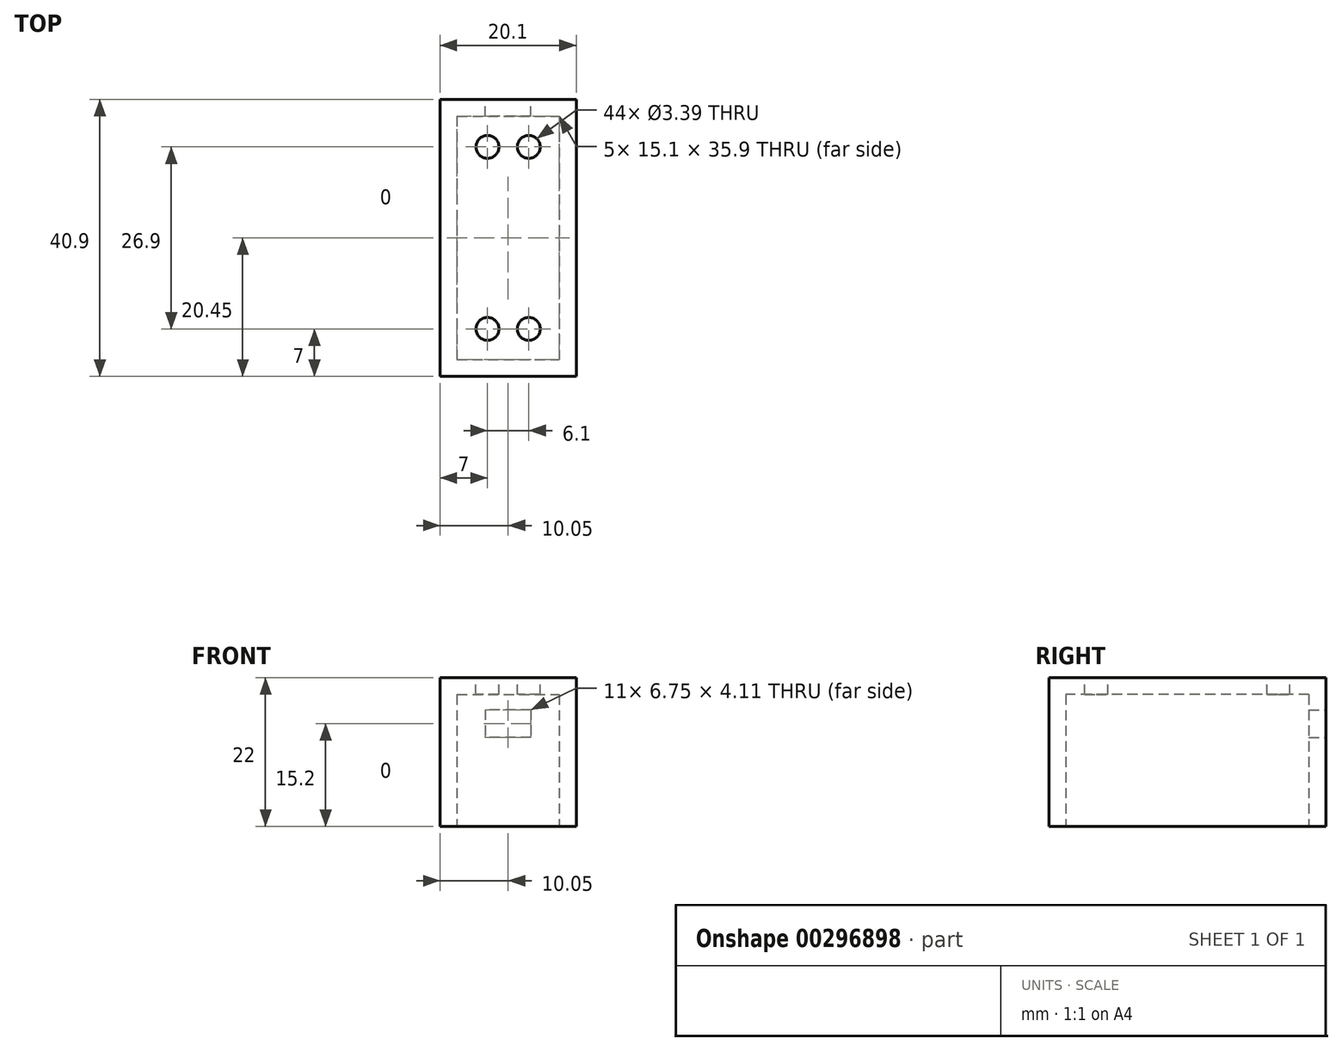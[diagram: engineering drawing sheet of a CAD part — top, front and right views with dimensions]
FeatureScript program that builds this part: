
annotation { "Feature Type Name" : "Feature", "Feature Type Description" : "" }
export const myFeature = defineFeature(function(context is Context, id is Id, definition is map)
    precondition{}
    {
        {
            var Q0;
            Q0=qCreatedBy(makeId("Top.planeOp"),FACE);
            var sketch = newSketch(context, id + "F0", { "sketchPlane" : qUnion([Q0])});
            skLineSegment(sketch, "E0", {"start": v(17.6, 44.65) * mm, "end": v(-2.5, 44.65) * mm});
            skLineSegment(sketch, "E1", {"start": v(17.6, 3.75) * mm, "end": v(-2.5, 3.75) * mm});
            skLineSegment(sketch, "E2", {"start": v(-2.5, 44.65) * mm, "end": v(-2.5, 3.75) * mm});
            skLineSegment(sketch, "E3", {"start": v(17.6, 44.65) * mm, "end": v(17.6, 3.75) * mm});
            skLineSegment(sketch, "E4.bottom", {"start": v(0, 42.15) * mm, "end": v(15.1, 42.15) * mm});
            skLineSegment(sketch, "E4.top", {"start": v(0, 6.25) * mm, "end": v(15.1, 6.25) * mm});
            skLineSegment(sketch, "E4.left", {"start": v(0, 42.15) * mm, "end": v(0, 6.25) * mm});
            skLineSegment(sketch, "E4.right", {"start": v(15.1, 42.15) * mm, "end": v(15.1, 6.25) * mm});
            skSolve(sketch);
        }
        {
            var Q0;
            Q0=makeQuery(id+"F0.imprint","IMPRINT",FACE,{"disambiguationData":[TD([[makeQuery(id+"F0.imprint","IMPRINT",EDGE,{"derivedFrom":sQuery(id+"F0.wireOp",EDGE,"E0")}),1.0]])]});
            var Q1;
            Q1=makeQuery(id+"F0.imprint","IMPRINT",FACE,{"disambiguationData":[TD([[makeQuery(id+"F0.imprint","IMPRINT",EDGE,{"derivedFrom":sQuery(id+"F0.wireOp",EDGE,"E4.bottom")}),-1.0]])]});
            extrude(context, id + "F1", {"entities" : qUnion([Q0, Q1]), "depth" : 22 * mm});
        }
        {
            var Q0;
            Q0=makeQuery(id+"F0.imprint","IMPRINT",FACE,{"disambiguationData":[TD([[makeQuery(id+"F0.imprint","IMPRINT",EDGE,{"derivedFrom":sQuery(id+"F0.wireOp",EDGE,"E4.bottom")}),-1.0]])]});
            extrude(context, id + "F2", {"entities" : qUnion([Q0]), "operationType" : NewBodyOperationType.REMOVE, "depth" : 19.5 * mm});
        }
        {
            var Q0;
            Q0=makeQuery(id+"F1.opExtrude","CAP_FACE",FACE,{"disambiguationData":[OSD([sQuery(id+"F0.wireOp",EDGE,"E0"),sQuery(id+"F0.wireOp",EDGE,"E1"),sQuery(id+"F0.wireOp",EDGE,"E2"),sQuery(id+"F0.wireOp",EDGE,"E3")])],"isStart":false});
            cPlane(context, id + "F3", {"entities" : qUnion([Q0]), "cplaneType" : CPlaneType.OFFSET, "offset" : 0 * mm, "width" : 150 * mm, "height" : 150 * mm});
        }
        {
            var Q0;
            Q0=qCreatedBy(id+"F3.planeOp",FACE);
            var sketch = newSketch(context, id + "F4", { "sketchPlane" : qUnion([Q0])});
            skLineSegment(sketch, "E5.bottom", {"start": v(10.6, 10.75) * mm, "end": v(4.5, 10.75) * mm, "construction": true});
            skLineSegment(sketch, "E5.top", {"start": v(10.6, 37.65) * mm, "end": v(4.5, 37.65) * mm, "construction": true});
            skLineSegment(sketch, "E5.left", {"start": v(10.6, 10.75) * mm, "end": v(10.6, 37.65) * mm, "construction": true});
            skLineSegment(sketch, "E5.right", {"start": v(4.5, 10.75) * mm, "end": v(4.5, 37.65) * mm, "construction": true});
            skCircle(sketch, "E6", {"center": v(4.5, 37.65) * mm, "radius": 1.7 * mm});
            skCircle(sketch, "E7", {"center": v(10.6, 37.65) * mm, "radius": 1.7 * mm});
            skCircle(sketch, "E8", {"center": v(4.5, 10.75) * mm, "radius": 1.7 * mm});
            skCircle(sketch, "E9", {"center": v(10.6, 10.75) * mm, "radius": 1.7 * mm});
            skSolve(sketch);
        }
        {
            var Q0;
            Q0 = qSketchRegion(id + "F4", true);
            extrude(context, id + "F5", {"entities" : qUnion([Q0]), "operationType" : NewBodyOperationType.REMOVE, "oppositeDirection" : true, "depth" : 25 * mm});
        }
        {
            var Q0;
            Q0=makeQuery(id+"F1.opExtrude","SWEPT_FACE",FACE,{"disambiguationData":[OSD([sQuery(id+"F0.wireOp",EDGE,"E0")])]});
            cPlane(context, id + "F6", {"entities" : qUnion([Q0]), "cplaneType" : CPlaneType.OFFSET, "offset" : 0 * mm, "width" : 150 * mm, "height" : 150 * mm});
        }
        {
            var Q0;
            Q0=qCreatedBy(id+"F6.planeOp",FACE);
            var sketch = newSketch(context, id + "F7", { "sketchPlane" : qUnion([Q0])});
            skPoint(sketch, "E10", {"position": v(-7.55, 15.2) * mm});
            skLineSegment(sketch, "E11.bottom", {"start": v(-7.55, 17.25) * mm, "end": v(-4.17, 17.25) * mm});
            skLineSegment(sketch, "E11.top", {"start": v(-7.55, 13.14) * mm, "end": v(-4.17, 13.14) * mm});
            skLineSegment(sketch, "E11.left", {"start": v(-7.55, 17.25) * mm, "end": v(-7.55, 13.14) * mm});
            skLineSegment(sketch, "E11.right", {"start": v(-4.17, 17.25) * mm, "end": v(-4.17, 13.14) * mm});
            skLineSegment(sketch, "E12.bottom", {"start": v(-7.55, 13.14) * mm, "end": v(-7.55, 13.14) * mm});
            skLineSegment(sketch, "E12.top", {"start": v(-7.55, 17.25) * mm, "end": v(-7.55, 17.25) * mm});
            skLineSegment(sketch, "E12.left", {"start": v(-7.55, 13.14) * mm, "end": v(-7.55, 17.25) * mm});
            skLineSegment(sketch, "E12.right", {"start": v(-7.55, 13.14) * mm, "end": v(-7.55, 17.25) * mm});
            skLineSegment(sketch, "E13.bottom", {"start": v(-7.55, 17.25) * mm, "end": v(-10.92, 17.25) * mm});
            skLineSegment(sketch, "E13.top", {"start": v(-7.55, 13.14) * mm, "end": v(-10.92, 13.14) * mm});
            skLineSegment(sketch, "E13.right", {"start": v(-10.92, 17.25) * mm, "end": v(-10.92, 13.14) * mm});
            skSolve(sketch);
        }
        {
            var Q0;
            Q0 = qSketchRegion(id + "F7", true);
            extrude(context, id + "F8", {"entities" : qUnion([Q0]), "operationType" : NewBodyOperationType.REMOVE, "oppositeDirection" : true, "depth" : 25 * mm});
        }
    });
